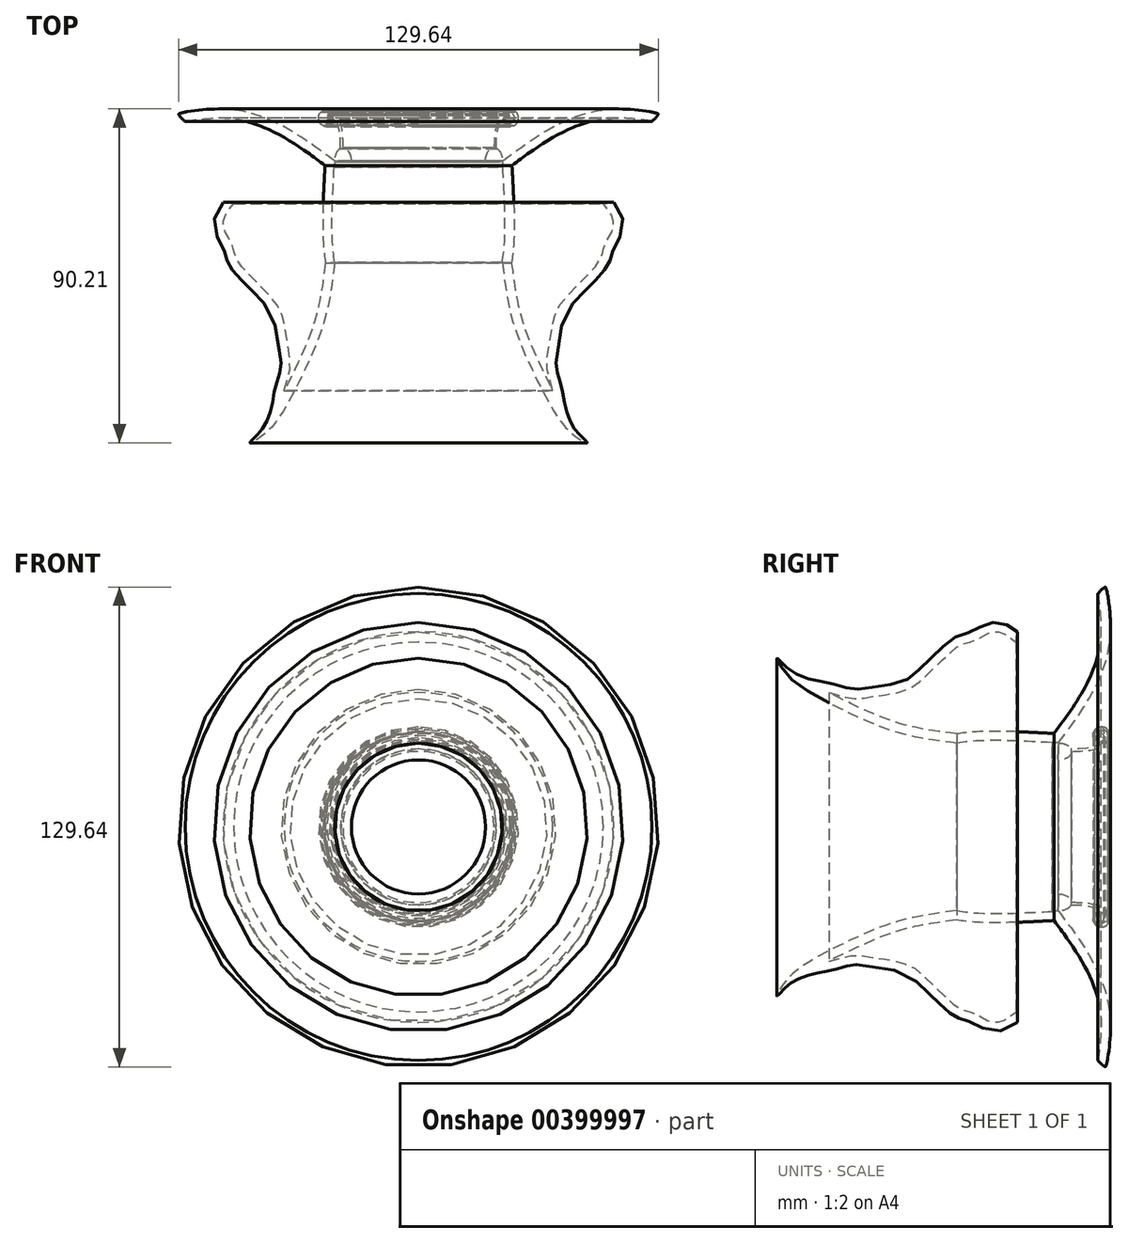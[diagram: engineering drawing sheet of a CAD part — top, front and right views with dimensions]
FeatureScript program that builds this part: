
annotation { "Feature Type Name" : "Feature", "Feature Type Description" : "" }
export const myFeature = defineFeature(function(context is Context, id is Id, definition is map)
    precondition{}
    {
        {
            var Q0;
            Q0=qCreatedBy(makeId("Top.planeOp"),FACE);
            var sketch = newSketch(context, id + "F0", { "sketchPlane" : qUnion([Q0])});
            skEllipticalArc(sketch, "E0", {});
            skEllipticalArc(sketch, "E1", {});
            skFitSpline(sketch, "E2", {"points": [v(2.3, 20.9) * mm, v(2.89, 0) * mm, v(1.74, -9.47) * mm], "startDerivative": vector(2.01, -38.53) * mm, "endDerivative": vector(-3.6, -21.18) * mm});
            skFitSpline(sketch, "E3", {"points": [v(-2.3, 20.9) * mm, v(-3.05, 0) * mm, v(-1.74, -9.47) * mm], "startDerivative": vector(-2.5, -38.54) * mm, "endDerivative": vector(4.14, -21.16) * mm});
            skEllipticalArc(sketch, "E4", {});
            skFitSpline(sketch, "E5", {"points": [v(-2.3, 20.9) * mm, v(0, 20.9) * mm, v(2.3, 20.9) * mm], "startDerivative": vector(4.7, -2.5) * mm, "endDerivative": vector(4.7, 2.5) * mm});
            skFitSpline(sketch, "E6", {"points": [v(-2.4, 19.25) * mm, v(0, 18.83) * mm, v(2.38, 19.24) * mm], "startDerivative": vector(4.9, -2.33) * mm, "endDerivative": vector(4.87, 2.3) * mm});
            skFitSpline(sketch, "E7", {"points": [v(2.3, 20.9) * mm, v(15.85, 30.1) * mm, v(32.92, 34.98) * mm, v(44.41, 33.58) * mm, v(36.58, 33.58) * mm, v(28.57, 33.06) * mm, v(16.1, 28.61) * mm, v(2.38, 19.24) * mm], "startDerivative": vector(81.12, 61.53) * mm, "endDerivative": vector(-77.6, -62.7) * mm});
            skFitSpline(sketch, "E8", {"points": [v(2.38, 19.24) * mm, v(12.47, 14.95) * mm, v(28.81, 10.34) * mm, v(32.38, 9.81) * mm, v(34.78, 10.9) * mm, v(36.24, 13.24) * mm, v(35.51, 15.87) * mm, v(36.39, 18.85) * mm, v(37.78, 20.9) * mm, v(38.21, 23.65) * mm, v(39.54, 26.37) * mm, v(41.1, 29.93) * mm, v(44.41, 33.58) * mm], "startDerivative": vector(70.32, -29.03) * mm, "endDerivative": vector(18.2, 40.24) * mm});
            skFitSpline(sketch, "E9", {"points": [v(2.22, -6.62) * mm, v(4.74, -21.24) * mm, v(9.72, -34.27) * mm, v(16.75, -47.59) * mm, v(22.16, -53.59) * mm, v(25.24, -55.2) * mm, v(22.5, -52.37) * mm, v(20.7, -49.53) * mm, v(19.34, -45.75) * mm, v(18.72, -42.23) * mm, v(17.47, -37.47) * mm, v(16.77, -34.04) * mm, v(17.42, -29.11) * mm, v(19.07, -20.9) * mm, v(22.35, -16.46) * mm, v(27.45, -11.2) * mm, v(31.06, -6.62) * mm, v(32.38, -2.5) * mm, v(34.51, 1.61) * mm, v(34.51, 6.21) * mm, v(32.38, 9.81) * mm], "startDerivative": vector(24.83, -191.18) * mm, "endDerivative": vector(-60.54, 80.48) * mm});
            skEllipse(sketch, "E10", {"center": v(28.24, 24.96) * mm, "majorRadius": 3.27 * mm, "minorRadius": 1.36 * mm, "majorAxis": v(0.84, 0.54)});
            skEllipse(sketch, "E11", {"center": v(28.24, 24.96) * mm, "majorRadius": 1.8 * mm, "minorRadius": 0.84 * mm, "majorAxis": v(0.82, 0.57)});
            skEllipse(sketch, "E12", {"center": v(24.15, 5.65) * mm, "majorRadius": 2.9 * mm, "minorRadius": 1.52 * mm, "majorAxis": v(0.82, -0.57)});
            skEllipse(sketch, "E13", {"center": v(24.15, 5.65) * mm, "majorRadius": 2.05 * mm, "minorRadius": 0.86 * mm, "majorAxis": v(0.76, -0.65)});
            skFitSpline(sketch, "E14", {"points": [v(2.22, -6.62) * mm, v(2.22, -6.56) * mm], "startDerivative": vector(0, 0.06) * mm, "endDerivative": vector(0, 0.06) * mm});
            skLineSegment(sketch, "E15", {"start": v(2.22, -6.56) * mm, "end": v(2.22, -6.55) * mm});
            skArc(sketch, "E16", {"start": v(3.2, 30.63) * mm, "mid": v(6.58, 31.93) * mm, "end": v(4.26, 34.7) * mm});
            skFitSpline(sketch, "E17", {"points": [v(0, 24.44) * mm, v(0.17, 27.52) * mm, v(0.46, 30.02) * mm, v(1.38, 32.67) * mm, v(2.86, 34.16) * mm, v(4.26, 34.7) * mm, v(5.9, 34.15) * mm, v(6.54, 33.17) * mm, v(6.42, 31.5) * mm, v(5.17, 30.4) * mm, v(3.2, 30.63) * mm, v(2.58, 32.37) * mm, v(3.43, 33.46) * mm, v(4.47, 33.63) * mm, v(5.32, 33.33) * mm, v(5.54, 32.83) * mm, v(5.46, 31.98) * mm, v(5, 31.43) * mm, v(4.06, 31.54) * mm, v(3.73, 32.07) * mm, v(4.64, 31.8) * mm, v(5.1, 32.7) * mm, v(4.5, 33.16) * mm, v(3.6, 33) * mm, v(3.02, 32.23) * mm, v(3.46, 31.08) * mm, v(5.02, 30.75) * mm, v(6.02, 31.63) * mm, v(6.13, 33.11) * mm, v(5.5, 33.9) * mm, v(4.27, 34.21) * mm, v(3.05, 33.74) * mm, v(1.87, 32.34) * mm, v(1.14, 29.93) * mm, v(0.72, 27.44) * mm, v(0.67, 24.28) * mm], "startDerivative": vector(3.76, 75.56) * mm, "endDerivative": vector(0.96, -77.04) * mm});
            skFitSpline(sketch, "E18", {"points": [v(2.38, 19.24) * mm, v(6.91, 21.58) * mm, v(16.42, 27.5) * mm, v(28.7, 31.98) * mm, v(36.58, 32.61) * mm, v(43.66, 33.11) * mm, v(36.58, 31.98) * mm, v(28.73, 31.35) * mm, v(16.53, 26.57) * mm, v(7.08, 21.11) * mm, v(2.38, 19.24) * mm]});
            skFitSpline(sketch, "E19", {"points": [v(3.89, 16) * mm, v(8, 13.7) * mm, v(12.47, 11.56) * mm, v(16.7, 10.04) * mm, v(24.01, 8.77) * mm, v(20.07, 8.11) * mm, v(20.15, 5.49) * mm, v(23.1, 2.28) * mm, v(26.97, 1.63) * mm, v(29.1, 2.7) * mm, v(27.05, 0.15) * mm, v(22.12, 1.05) * mm, v(18.5, 4.91) * mm, v(17.52, 7.43) * mm, v(12.47, 9.76) * mm, v(7.59, 12.3) * mm, v(3.89, 16) * mm]});
            skFitSpline(sketch, "E20", {"points": [v(5.46, 9.78) * mm, v(10.98, 6.1) * mm, v(15.51, 2.9) * mm, v(19.7, -3.33) * mm, v(18.04, -7.97) * mm, v(12.47, -7.2) * mm, v(12.47, -2.77) * mm, v(15.68, -3.9) * mm, v(13.83, -5.32) * mm, v(17.46, -5.96) * mm, v(17.35, -3.33) * mm, v(14.6, 0) * mm, v(9.86, 0) * mm, v(8.99, -8.85) * mm, v(10.9, -14.68) * mm, v(14.72, -14.4) * mm, v(16.47, -12.87) * mm, v(12.47, -19.72) * mm, v(12.04, -24.36) * mm, v(10.55, -27.84) * mm, v(8.92, -21.48) * mm, v(8.26, -16.46) * mm, v(7.13, -8.6) * mm, v(6.38, 0) * mm, v(6.08, 2.9) * mm, v(5.85, 7.32) * mm, v(5.46, 9.78) * mm]});
            skPoint(sketch, "E21.6.internal.snap0", {"position": v(27.52, 26.1) * mm});
            skFitSpline(sketch, "E21", {"points": [v(7.6, 19.77) * mm, v(15.95, 23.96) * mm, v(21.25, 26.36) * mm, v(24.34, 28.44) * mm, v(23.14, 24.47) * mm, v(23.41, 22.07) * mm, v(27.52, 21.38) * mm, v(29.13, 21.66) * mm, v(27.1, 19.54) * mm, v(23.04, 18.8) * mm, v(17.7, 18.9) * mm, v(12.3, 19.08) * mm, v(7.6, 19.77) * mm]});
            skFitSpline(sketch, "E22.MirrorCS", {"points": [v(-2.22, -6.62) * mm, v(-2.22, -6.56) * mm], "startDerivative": vector(0, 0.06) * mm, "endDerivative": vector(0, 0.06) * mm});
            skLineSegment(sketch, "E23.MirrorCS", {"start": v(-2.22, -6.56) * mm, "end": v(-2.22, -6.55) * mm});
            skEllipticalArc(sketch, "E24.MirrorCS", {});
            skEllipticalArc(sketch, "E25.MirrorCS", {});
            skFitSpline(sketch, "E26.MirrorCS", {"points": [v(2.3, 20.9) * mm, v(0, 20.9) * mm, v(-2.3, 20.9) * mm], "startDerivative": vector(-4.7, -2.5) * mm, "endDerivative": vector(-4.7, 2.5) * mm});
            skFitSpline(sketch, "E27.MirrorCS", {"points": [v(2.4, 19.25) * mm, v(0, 18.83) * mm, v(-2.38, 19.24) * mm], "startDerivative": vector(-4.9, -2.33) * mm, "endDerivative": vector(-4.87, 2.3) * mm});
            skEllipticalArc(sketch, "E28.MirrorCS", {});
            skLineSegment(sketch, "E29", {"start": v(-20.4, 52.86) * mm, "end": v(-20.4, -60.76) * mm});
            skPoint(sketch, "E30.orphan", {"position": v(0, 43.1) * mm});
            const initialGuessF0  = {"E0": [0, 0.02090463444890858, 0, -1, 0.0035310519394098046, 0.002297039903684678, 1.5707963267948966, 4.71238898038469], "E1": [0, -0.009469367382299913, 0, 1, 0.0035901373358472096, 0.001739675895624183, 1.5707963267948966, 4.71238898038469], "E4": [0.001387894892873516, 0.023718264862181527, 0.3162766123089874, -0.9486670145558718, 0.0018780809074936957, 0.0005518705882354958, 4.293777265012078, 0.42567047345905185], "E24.MirrorCS": [0, 0.02090463444890858, 0, -1, 0.0035310519394098046, 0.002297039903684678, 1.5707963267948966, 4.71238898038469], "E25.MirrorCS": [-0.001387894892873516, 0.023718264862181527, -0.3162766123089874, -0.9486670145558718, 0.0018780809074936957, 0.0005518705882354958, 5.8575148337205345, 1.9894080421675087], "E28.MirrorCS": [0, -0.009469367382299913, 0, 1, 0.0035901373358472096, 0.001739675895624183, 1.5707963267948966, 4.71238898038469]};
            skSetInitialGuess(sketch, initialGuessF0);
            skSolve(sketch);
        }
        {
            var Q0;
            Q0=makeQuery(id+"F0.imprint","IMPRINT",FACE,{"disambiguationData":[TD([[makeQuery(id+"F0.imprint","IMPRINT",EDGE,{"derivedFrom":sQuery(id+"F0.wireOp",EDGE,"E10")}),-1.0]])]});
            var Q1;
            Q1=makeQuery(id+"F0.imprint","IMPRINT",FACE,{"disambiguationData":[TD([[makeQuery(id+"F0.imprint","IMPRINT",EDGE,{"derivedFrom":sQuery(id+"F0.wireOp",EDGE,"E19")}),-1.0]])]});
            var Q2;
            Q2=makeQuery(id+"F0.imprint","IMPRINT",FACE,{"disambiguationData":[TD([[makeQuery(id+"F0.imprint","IMPRINT",EDGE,{"derivedFrom":sQuery(id+"F0.wireOp",EDGE,"E20")}),-1.0]])]});
            var Q3;
            Q3=makeQuery(id+"F0.imprint","IMPRINT",FACE,{"disambiguationData":[TD([[makeQuery(id+"F0.imprint","IMPRINT",EDGE,{"derivedFrom":sQuery(id+"F0.wireOp",EDGE,"E21")}),-1.0]])]});
            var Q4;
            {var subQ0=sQuery(id+"F0.wireOp",EDGE,"E9");Q4=makeQuery(id+"F0.imprint","IMPRINT",FACE,{"disambiguationData":[TD([[makeQuery(id+"F0.imprint","IMPRINT",EDGE,{"derivedFrom":subQ0}),1.0]])]});}
            var Q5;
            {var subQ1=sQuery(id+"F0.wireOp",EDGE,"E7");var subQ5=makeQuery(id+"F0.imprint","INTERSECT",VERTEX,{"derivedFrom":[subQ1,sQuery(id+"F0.wireOp",EDGE,"E8")]});Q5=makeQuery(id+"F0.imprint","IMPRINT",FACE,{"disambiguationData":[TD([[makeQuery(id+"F0.imprint","IMPRINT",EDGE,{"disambiguationData":[TD([[subQ5,-1.0]])],"derivedFrom":subQ1}),-1.0]])]});}
            var Q6;
            {var subQ0=sQuery(id+"F0.wireOp",EDGE,"E28.MirrorCS");Q6=makeQuery(id+"F0.imprint","IMPRINT",FACE,{"disambiguationData":[TD([[makeQuery(id+"F0.imprint","IMPRINT",EDGE,{"derivedFrom":subQ0}),1.0]])]});}
            var Q7;
            Q7=makeQuery(id+"F0.imprint","IMPRINT",FACE,{"disambiguationData":[TD([[makeQuery(id+"F0.imprint","IMPRINT",EDGE,{"derivedFrom":sQuery(id+"F0.wireOp",EDGE,"E10")}),1.0]])]});
            var Q8;
            Q8=makeQuery(id+"F0.imprint","IMPRINT",FACE,{"disambiguationData":[TD([[makeQuery(id+"F0.imprint","IMPRINT",EDGE,{"derivedFrom":sQuery(id+"F0.wireOp",EDGE,"E12")}),1.0]])]});
            var Q9;
            {var subQ0=sQuery(id+"F0.wireOp",EDGE,"E7");var subQ1=makeQuery(id+"F0.imprint","INTERSECT",VERTEX,{"derivedFrom":[subQ0,sQuery(id+"F0.wireOp",EDGE,"E27.MirrorCS")]});Q9=makeQuery(id+"F0.imprint","IMPRINT",FACE,{"disambiguationData":[TD([[makeQuery(id+"F0.imprint","IMPRINT",EDGE,{"disambiguationData":[TD([[subQ1,1.0]])],"derivedFrom":subQ0}),1.0]])]});}
            var Q10;
            {var subQ0=sQuery(id+"F0.wireOp",EDGE,"E17");var subQ1=sQuery(id+"F0.wireOp",EDGE,"E16");var subQ10=makeQuery(id+"F0.imprint","INTERSECT",VERTEX,{"disambiguationData":[OD(0.0)],"derivedFrom":[subQ1,subQ0]});Q10=makeQuery(id+"F0.imprint","IMPRINT",FACE,{"disambiguationData":[TD([[makeQuery(id+"F0.imprint","IMPRINT",EDGE,{"disambiguationData":[TD([[subQ10,-1.0]])],"derivedFrom":subQ1}),1.0]])]});}
            var Q11;
            Q11=makeQuery(id+"F0.imprint","IMPRINT",FACE,{"disambiguationData":[TD([[makeQuery(id+"F0.imprint","IMPRINT",EDGE,{"derivedFrom":sQuery(id+"F0.wireOp",EDGE,"E11")}),1.0]])]});
            var Q12;
            Q12=makeQuery(id+"F0.imprint","IMPRINT",FACE,{"disambiguationData":[TD([[makeQuery(id+"F0.imprint","IMPRINT",EDGE,{"derivedFrom":sQuery(id+"F0.wireOp",EDGE,"E13")}),1.0]])]});
            var Q13;
            {var subQ0=sQuery(id+"F0.wireOp",EDGE,"E4");Q13=makeQuery(id+"F0.imprint","IMPRINT",FACE,{"disambiguationData":[TD([[makeQuery(id+"F0.imprint","IMPRINT",EDGE,{"derivedFrom":subQ0}),1.0]])]});}
            var Q14;
            {var subQ0=sQuery(id+"F0.wireOp",EDGE,"E17");var subQ1=sQuery(id+"F0.wireOp",EDGE,"E16");var subQ2=makeQuery(id+"F0.imprint","INTERSECT",VERTEX,{"disambiguationData":[OD(3.0)],"derivedFrom":[subQ1,subQ0]});Q14=makeQuery(id+"F0.imprint","IMPRINT",FACE,{"disambiguationData":[TD([[makeQuery(id+"F0.imprint","IMPRINT",EDGE,{"disambiguationData":[TD([[subQ2,-1.0]])],"derivedFrom":subQ1}),-1.0]])]});}
            var Q15;
            {var subQ0=sQuery(id+"F0.wireOp",EDGE,"E17");var subQ1=sQuery(id+"F0.wireOp",EDGE,"E16");var subQ2=makeQuery(id+"F0.imprint","INTERSECT",VERTEX,{"disambiguationData":[OD(4.0)],"derivedFrom":[subQ1,subQ0]});Q15=makeQuery(id+"F0.imprint","IMPRINT",FACE,{"disambiguationData":[TD([[makeQuery(id+"F0.imprint","IMPRINT",EDGE,{"disambiguationData":[TD([[subQ2,-1.0]])],"derivedFrom":subQ1}),1.0]])]});}
            var Q16;
            {var subQ0=sQuery(id+"F0.wireOp",EDGE,"E17");var subQ1=sQuery(id+"F0.wireOp",EDGE,"E16");var subQ2=makeQuery(id+"F0.imprint","INTERSECT",VERTEX,{"disambiguationData":[OD(5.0)],"derivedFrom":[subQ1,subQ0]});Q16=makeQuery(id+"F0.imprint","IMPRINT",FACE,{"disambiguationData":[TD([[makeQuery(id+"F0.imprint","IMPRINT",EDGE,{"disambiguationData":[TD([[subQ2,-1.0]])],"derivedFrom":subQ1}),-1.0]])]});}
            var Q17;
            {var subQ0=sQuery(id+"F0.wireOp",EDGE,"E17");var subQ1=sQuery(id+"F0.wireOp",EDGE,"E16");var subQ2=makeQuery(id+"F0.imprint","INTERSECT",VERTEX,{"disambiguationData":[OD(0.0)],"derivedFrom":[subQ1,subQ0]});Q17=makeQuery(id+"F0.imprint","IMPRINT",FACE,{"disambiguationData":[TD([[makeQuery(id+"F0.imprint","IMPRINT",EDGE,{"disambiguationData":[TD([[subQ2,-1.0]])],"derivedFrom":subQ1}),-1.0]])]});}
            var Q18;
            {var subQ0=sQuery(id+"F0.wireOp",EDGE,"E17");var subQ1=sQuery(id+"F0.wireOp",EDGE,"E16");var subQ2=makeQuery(id+"F0.imprint","INTERSECT",VERTEX,{"disambiguationData":[OD(2.0)],"derivedFrom":[subQ1,subQ0]});Q18=makeQuery(id+"F0.imprint","IMPRINT",FACE,{"disambiguationData":[TD([[makeQuery(id+"F0.imprint","IMPRINT",EDGE,{"disambiguationData":[TD([[subQ2,-1.0]])],"derivedFrom":subQ1}),1.0]])]});}
            var Q19;
            {var subQ0=sQuery(id+"F0.wireOp",EDGE,"E17");var subQ1=sQuery(id+"F0.wireOp",EDGE,"E16");var subQ2=makeQuery(id+"F0.imprint","INTERSECT",VERTEX,{"disambiguationData":[OD(1.0)],"derivedFrom":[subQ1,subQ0]});Q19=makeQuery(id+"F0.imprint","IMPRINT",FACE,{"disambiguationData":[TD([[makeQuery(id+"F0.imprint","IMPRINT",EDGE,{"disambiguationData":[TD([[subQ2,1.0]])],"derivedFrom":subQ1}),1.0]])]});}
            var Q20;
            {var subQ5=sQuery(id+"F0.wireOp",EDGE,"E4");Q20=makeQuery(id+"F0.imprint","IMPRINT",FACE,{"disambiguationData":[TD([[makeQuery(id+"F0.imprint","IMPRINT",EDGE,{"derivedFrom":subQ5}),-1.0]])]});}
            var Q21;
            {var subQ0=sQuery(id+"F0.wireOp",EDGE,"E25.MirrorCS");Q21=makeQuery(id+"F0.imprint","IMPRINT",FACE,{"disambiguationData":[TD([[makeQuery(id+"F0.imprint","IMPRINT",EDGE,{"derivedFrom":subQ0}),1.0]])]});}
            var Q22;
            {var subQ0=sQuery(id+"F0.wireOp",EDGE,"E26.MirrorCS");Q22=makeQuery(id+"F0.imprint","IMPRINT",FACE,{"disambiguationData":[TD([[makeQuery(id+"F0.imprint","IMPRINT",EDGE,{"derivedFrom":subQ0}),1.0]])]});}
            var Q23;
            {var subQ0=sQuery(id+"F0.wireOp",EDGE,"E27.MirrorCS");var subQ1=sQuery(id+"F0.wireOp",EDGE,"E2");var subQ2=makeQuery(id+"F0.imprint","INTERSECT",VERTEX,{"derivedFrom":[subQ1,subQ0]});Q23=makeQuery(id+"F0.imprint","IMPRINT",FACE,{"disambiguationData":[TD([[makeQuery(id+"F0.imprint","IMPRINT",EDGE,{"disambiguationData":[TD([[subQ2,-1.0]])],"derivedFrom":subQ1}),-1.0]])]});}
            var Q24;
            {var subQ0=sQuery(id+"F0.wireOp",EDGE,"E27.MirrorCS");var subQ1=sQuery(id+"F0.wireOp",EDGE,"E7");var subQ2=makeQuery(id+"F0.imprint","INTERSECT",VERTEX,{"derivedFrom":[subQ1,subQ0]});Q24=makeQuery(id+"F0.imprint","IMPRINT",FACE,{"disambiguationData":[TD([[makeQuery(id+"F0.imprint","IMPRINT",EDGE,{"disambiguationData":[TD([[subQ2,1.0]])],"derivedFrom":subQ1}),-1.0]])]});}
            var Q25;
            {var subQ0=sQuery(id+"F0.wireOp",EDGE,"E18");var subQ1=sQuery(id+"F0.wireOp",EDGE,"E2");var subQ3=makeQuery(id+"F0.imprint","INTERSECT",VERTEX,{"derivedFrom":[subQ1,subQ0]});Q25=makeQuery(id+"F0.imprint","IMPRINT",FACE,{"disambiguationData":[TD([[makeQuery(id+"F0.imprint","IMPRINT",EDGE,{"disambiguationData":[TD([[subQ3,-1.0]])],"derivedFrom":subQ1}),-1.0]])]});}
            var Q26;
            {var subQ0=sQuery(id+"F0.wireOp",EDGE,"E18");var subQ1=sQuery(id+"F0.wireOp",EDGE,"E8");var subQ3=makeQuery(id+"F0.imprint","INTERSECT",VERTEX,{"derivedFrom":[subQ1,subQ0]});Q26=makeQuery(id+"F0.imprint","IMPRINT",FACE,{"disambiguationData":[TD([[makeQuery(id+"F0.imprint","IMPRINT",EDGE,{"disambiguationData":[TD([[subQ3,1.0]])],"derivedFrom":subQ1}),-1.0]])]});}
            var Q27;
            {var subQ0=sQuery(id+"F0.wireOp",EDGE,"E18");var subQ2=sQuery(id+"F0.wireOp",EDGE,"E2");var subQ4=makeQuery(id+"F0.imprint","INTERSECT",VERTEX,{"derivedFrom":[subQ2,subQ0]});Q27=makeQuery(id+"F0.imprint","IMPRINT",FACE,{"disambiguationData":[TD([[makeQuery(id+"F0.imprint","IMPRINT",EDGE,{"disambiguationData":[TD([[subQ4,-1.0]])],"derivedFrom":subQ0}),-1.0]])]});}
            var Q28;
            {var subQ0=sQuery(id+"F0.wireOp",EDGE,"E27.MirrorCS");var subQ1=sQuery(id+"F0.wireOp",EDGE,"E2");var subQ2=makeQuery(id+"F0.imprint","INTERSECT",VERTEX,{"derivedFrom":[subQ1,subQ0]});Q28=makeQuery(id+"F0.imprint","IMPRINT",FACE,{"disambiguationData":[TD([[makeQuery(id+"F0.imprint","IMPRINT",EDGE,{"disambiguationData":[TD([[subQ2,-1.0]])],"derivedFrom":subQ1}),1.0]])]});}
            var Q29;
            Q29=sQuery(id+"F0.wireOp",EDGE,"E29");
            revolve(context, id + "F1", {"entities" : qUnion([Q0, Q1, Q2, Q3, Q4, Q5, Q6, Q7, Q8, Q9, Q10, Q11, Q12, Q13, Q14, Q15, Q16, Q17, Q18, Q19, Q20, Q21, Q22, Q23, Q24, Q25, Q26, Q27, Q28]), "axis" : qUnion([Q29]), "revolveType" : RevolveType.FULL});
        }
        {
            var Q0;
            Q0=makeQuery(id+"F1.opRevolve","SWEPT_FACE",FACE,{"disambiguationData":[OSD([sQuery(id+"F0.wireOp",EDGE,"E8")])]});
            shell(context, id + "F2", {"entities" : qUnion([Q0]), "thickness" : 2.5 * mm});
        }
    });
